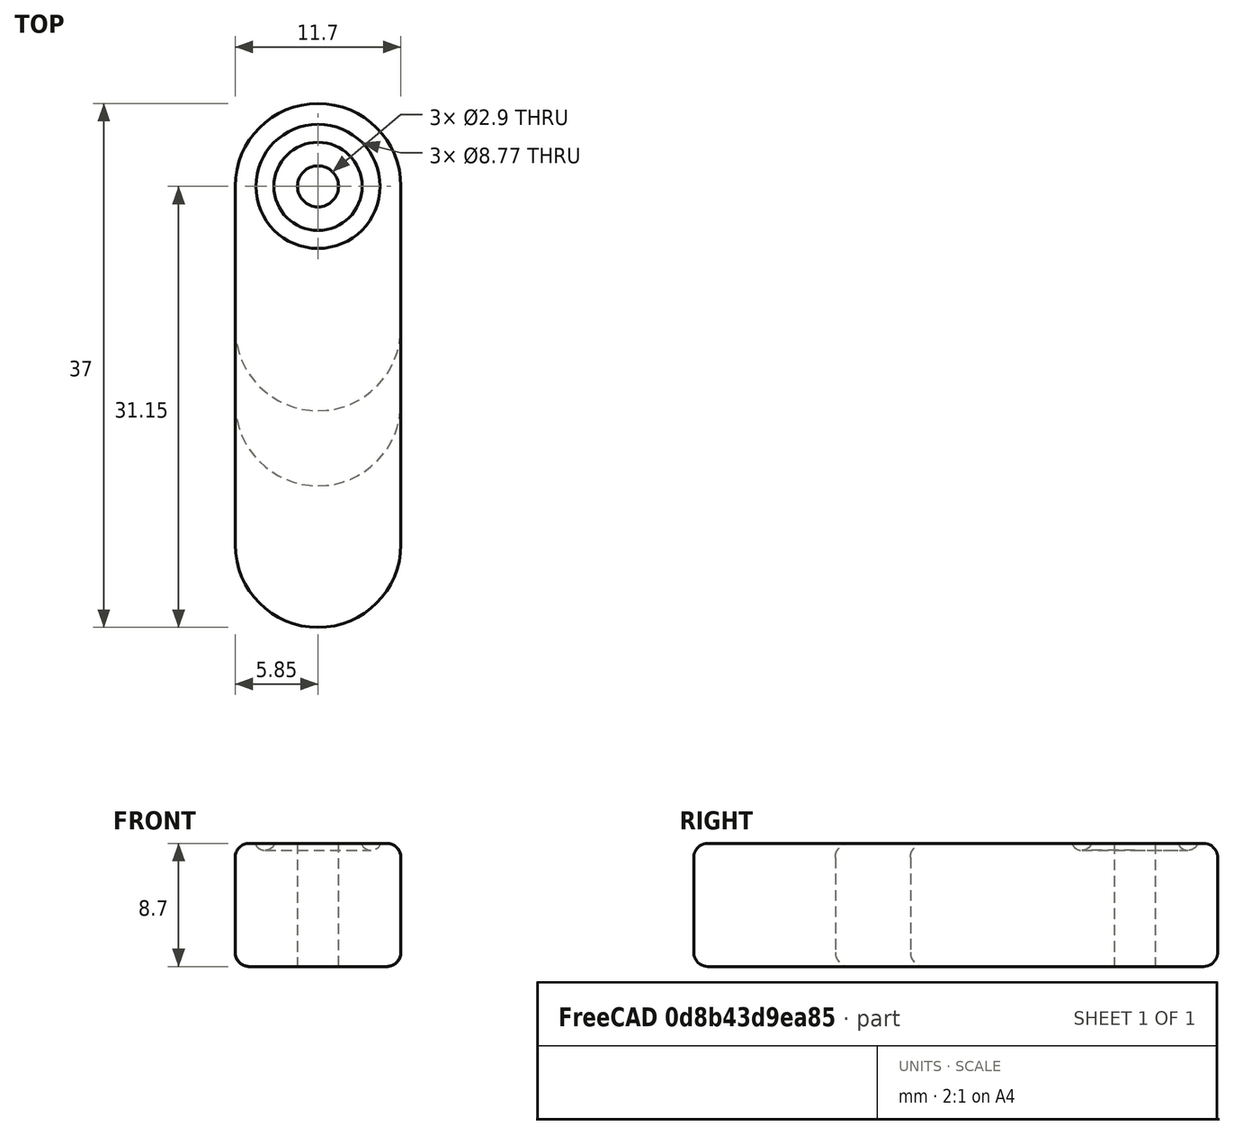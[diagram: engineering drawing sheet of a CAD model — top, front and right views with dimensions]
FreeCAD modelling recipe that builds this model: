
FCSTD DOCUMENT  (FreeCAD 1.0R39109 (Git))
Label: leg_very_small_six
License: All rights reserved
LicenseURL: http://en.wikipedia.org/wiki/All_rights_reserved
objects: Mesh::Feature×24, Sketcher::SketchObject×12, PartDesign::Groove×6, PartDesign::Fillet×6, PartDesign::Pad×3, PartDesign::Pocket×3, PartDesign::Body×3
note: 81 computed .brp shape members not serialized (recipe doc carries the construction recipe); baked Part::Feature solids carry a one-line shape summary decoded from their .brp

FEATURE [Sketcher::SketchObject] Sketch
  ArcFitTolerance = 0
  AttachmentSupport = -> [XY_Plane]
  FullyConstrained = true
  MakeInternals = false
  MapMode = 5
  sketch-geometry (4):
    g0: ArcOfCircle CenterX=0 CenterY=0 CenterZ=0 NormalX=0 NormalY=0 NormalZ=1 AngleXU=0 Radius=5.85 StartAngle=0 EndAngle=3.14159
    g1: LineSegment StartX=-5.85 StartY=7e-16 StartZ=0 EndX=-5.85 EndY=-10 EndZ=0
    g2: LineSegment StartX=5.85 StartY=0 StartZ=0 EndX=5.85 EndY=-10 EndZ=0
    g3: ArcOfCircle CenterX=3e-16 CenterY=-10 CenterZ=0 NormalX=0 NormalY=0 NormalZ=1 AngleXU=0 Radius=5.85 StartAngle=3.14159 EndAngle=6.28319
  constraints (12):
    c: Coincident(g0,g-1)
    c: PointOnObject(g0,g-1)
    c: PointOnObject(g0,g-1)
    c: Diameter(g0) = 11.7
    c: Coincident(g1,g0)
    c: Vertical(g1)
    c: Coincident(g2,g0)
    c: Vertical(g2)
    c: Equal(g2,g1)
    c: DistanceY(g1,g0) = 10
    c: Tangent(g1,g3) = -1.5708
    c: Coincident(g3,g2)
FEATURE [PartDesign::Pad] Pad
  Direction = (0,0,1)
  Length = 8.7
  Length2 = 10
  Profile = -> Sketch
  ReferenceAxis = -> Sketch [N_Axis]
  Suppressed = false
  Type = 0
FEATURE [Sketcher::SketchObject] Sketch001
  ArcFitTolerance = 0
  AttachmentSupport = -> [XY_Plane]
  FullyConstrained = true
  MakeInternals = false
  MapMode = 5
  sketch-geometry (1):
    g0: Circle CenterX=0 CenterY=0 CenterZ=0 NormalX=0 NormalY=0 NormalZ=1 AngleXU=0 Radius=1.45
  constraints (2):
    c: Coincident(g0,g-1)
    c: Diameter(g0) = 2.9
FEATURE [PartDesign::Pocket] Pocket
  BaseFeature = -> Pad
  Direction = (0,0,1)
  Length = 5
  Length2 = 5
  Profile = -> Sketch001
  ReferenceAxis = -> Sketch001 [N_Axis]
  Suppressed = false
  Type = 1
  UseCustomVector = true
FEATURE [Sketcher::SketchObject] Sketch002  label="elipse"
  ArcFitTolerance = 0
  AttachmentSupport = -> [XZ_Plane]
  FullyConstrained = true
  MakeInternals = false
  MapMode = 5
  Placement = pos=(0,0,0) rot=(1,0,0;1.5708rad)
  expr: Constraints[29] = 7.5 / 2
  sketch-geometry (13):
    g0: Circle [constr] CenterX=3.75 CenterY=8.7 CenterZ=0 NormalX=0 NormalY=0 NormalZ=1 AngleXU=0 Radius=0.5
    g1: LineSegment [constr] StartX=2.06 StartY=8.7 StartZ=0 EndX=5.44 EndY=8.7 EndZ=0
    g2: LineSegment [constr] StartX=3.75 StartY=6.89867 StartZ=0 EndX=3.75 EndY=10.0128 EndZ=0
    g3-g6: Circle [constr] x4 (B-spline internal-alignment scaffolding for g7; pole/knot coordinates omitted)
    g7: BSplineCurve PolesCount=4 KnotsCount=5 Degree=3 IsPeriodic=1
    g8-g12: GeomPoint [constr] x5 (B-spline internal-alignment scaffolding for g7; pole/knot coordinates omitted)
  constraints (23):
    c: Diameter(g0) = 1
    c: Horizontal(g1)
    c: PointOnObject(g0,g1)
    c: PointOnObject(g0,g2)
    c: Weight(g3) = 1
    c: PointOnObject(g3,g2)
    c: Equal(g3,g4)
    c: PointOnObject(g4,g1)
    c: Equal(g3,g5)
    c: PointOnObject(g5,g2)
    c: Equal(g3,g6)
    c: InternalAlignment(g3-g6 -> g7) x4
    c: InternalAlignment(g8-g12 -> g7) x5
    c: Symmetric(g1,g1,g2)
    c: Symmetric(g4,g6,g2)
    c: PointOnObject(g9,g0)
    c: Distance(g6,g3) = 1
    c: Distance(g11,g0) = 0.2
    c: Distance(g1,g2) = 2.47
    c: Distance(g2,g1) = 2.14
    c: Distance(g1,g0) = 1.69
    c: DistanceY(g-1,g0) = 8.7
    c: DistanceX(g-1,g0) = 3.75
FEATURE [PartDesign::Groove] Groove
  Angle = 360
  Angle2 = 60
  Axis = (0,2e-16,1)
  Base = (0,0,0)
  BaseFeature = -> Pocket
  Profile = -> Sketch002
  ReferenceAxis = -> Sketch002 [V_Axis]
  Suppressed = false
  Type = 0
FEATURE [Sketcher::SketchObject] Sketch003  label="rectangle"
  ArcFitTolerance = 0
  AttachmentSupport = -> [XZ_Plane]
  ExternalGeometry = -> [Sketch002]
  FullyConstrained = true
  MakeInternals = false
  MapMode = 5
  Placement = pos=(0,0,0) rot=(1,0,0;1.5708rad)
  sketch-geometry (4):
    g0: LineSegment StartX=3.11404 StartY=9.125 StartZ=0 EndX=4.38596 EndY=9.125 EndZ=0
    g1: LineSegment StartX=4.38596 StartY=9.125 StartZ=0 EndX=4.38596 EndY=8.625 EndZ=0
    g2: LineSegment StartX=4.38596 StartY=8.625 StartZ=0 EndX=3.11404 EndY=8.625 EndZ=0
    g3: LineSegment StartX=3.11404 StartY=8.625 StartZ=0 EndX=3.11404 EndY=9.125 EndZ=0
  constraints (11):
    c: Coincident(g0,g1)
    c: Coincident(g1,g2)
    c: Coincident(g2,g3)
    c: Coincident(g3,g0)
    c: Horizontal(g0)
    c: Horizontal(g2)
    c: Vertical(g1)
    c: Vertical(g3)
    c: Distance(g3) = 0.5
    c: Coincident(g2,g-3)
    c: PointOnObject(g1,g-3)
FEATURE [PartDesign::Groove] Groove001
  Angle = 360
  Angle2 = 60
  Axis = (0,2e-16,1)
  Base = (0,0,0)
  BaseFeature = -> Groove
  Profile = -> Sketch003
  ReferenceAxis = -> Sketch003 [V_Axis]
  Suppressed = false
  Type = 0
FEATURE [PartDesign::Fillet] Fillet
  Base = -> Groove001 [Edge10]
  BaseFeature = -> Groove001
  Radius = 1
  SupportTransform = false
  Suppressed = false
  UseAllEdges = false
FEATURE [PartDesign::Fillet] Fillet001
  Base = -> Fillet [Edge12]
  BaseFeature = -> Fillet
  Radius = 1
  SupportTransform = false
  Suppressed = false
  UseAllEdges = false
FEATURE [PartDesign::Body] Body  label="leg_22mm"
  AllowCompound = false
  Group = -> [Sketch,Pad,Sketch001,Pocket,Sketch002,Groove,Sketch003,Groove001,Fillet,Fillet001]
  Origin = -> Origin
  Tip = -> Fillet001
FEATURE [Mesh::Feature] Mesh  label="leg_22 001"
FEATURE [Mesh::Feature] Mesh001  label="leg_22 002"
  Placement = pos=(15,0,0) rot=(0,0,1;0rad)
FEATURE [Mesh::Feature] Mesh002  label="leg_22 003"
  Placement = pos=(30,0,0) rot=(0,0,1;0rad)
FEATURE [Mesh::Feature] Mesh003  label="leg_22 004"
  Placement = pos=(0,24,0) rot=(0,0,1;0rad)
FEATURE [Mesh::Feature] Mesh004  label="leg_22 005"
  Placement = pos=(15,24,0) rot=(0,0,1;0rad)
FEATURE [Mesh::Feature] Mesh005  label="leg_22 006"
  Placement = pos=(30,24,0) rot=(0,0,1;0rad)
FEATURE [Sketcher::SketchObject] Sketch004
  ArcFitTolerance = 0
  AttachmentSupport = -> [XY_Plane001]
  FullyConstrained = true
  MakeInternals = false
  MapMode = 5
  sketch-geometry (4):
    g0: ArcOfCircle CenterX=0 CenterY=0 CenterZ=0 NormalX=0 NormalY=0 NormalZ=1 AngleXU=0 Radius=5.85 StartAngle=0 EndAngle=3.14159
    g1: LineSegment StartX=-5.85 StartY=7e-16 StartZ=0 EndX=-5.85 EndY=-15.3 EndZ=0
    g2: LineSegment StartX=5.85 StartY=0 StartZ=0 EndX=5.85 EndY=-15.3 EndZ=0
    g3: ArcOfCircle CenterX=1.355e-13 CenterY=-15.3 CenterZ=0 NormalX=0 NormalY=0 NormalZ=1 AngleXU=0 Radius=5.85 StartAngle=3.14159 EndAngle=6.28319
  constraints (12):
    c: Coincident(g0,g-1)
    c: PointOnObject(g0,g-1)
    c: PointOnObject(g0,g-1)
    c: Diameter(g0) = 11.7
    c: Coincident(g1,g0)
    c: Vertical(g1)
    c: Coincident(g2,g0)
    c: Vertical(g2)
    c: Equal(g2,g1)
    c: DistanceY(g1,g0) = 15.3
    c: Tangent(g1,g3) = -1.5708
    c: Coincident(g3,g2)
FEATURE [PartDesign::Pad] Pad001
  Direction = (0,0,1)
  Length = 8.7
  Length2 = 10
  Profile = -> Sketch004
  ReferenceAxis = -> Sketch004 [N_Axis]
  Suppressed = false
  Type = 0
FEATURE [Sketcher::SketchObject] Sketch005
  ArcFitTolerance = 0
  AttachmentSupport = -> [XY_Plane001]
  FullyConstrained = true
  MakeInternals = false
  MapMode = 5
  sketch-geometry (1):
    g0: Circle CenterX=0 CenterY=0 CenterZ=0 NormalX=0 NormalY=0 NormalZ=1 AngleXU=0 Radius=1.45
  constraints (2):
    c: Coincident(g0,g-1)
    c: Diameter(g0) = 2.9
FEATURE [PartDesign::Pocket] Pocket001
  BaseFeature = -> Pad001
  Direction = (0,0,1)
  Length = 5
  Length2 = 5
  Profile = -> Sketch005
  ReferenceAxis = -> Sketch005 [N_Axis]
  Suppressed = false
  Type = 1
  UseCustomVector = true
FEATURE [Sketcher::SketchObject] Sketch006  label="elipse001"
  ArcFitTolerance = 0
  AttachmentSupport = -> [XZ_Plane001]
  FullyConstrained = true
  MakeInternals = false
  MapMode = 5
  Placement = pos=(0,0,0) rot=(1,0,0;1.5708rad)
  expr: Constraints[29] = 7.5 / 2
  sketch-geometry (13):
    g0: Circle [constr] CenterX=3.75 CenterY=8.7 CenterZ=0 NormalX=0 NormalY=0 NormalZ=1 AngleXU=0 Radius=0.5
    g1: LineSegment [constr] StartX=2.06 StartY=8.7 StartZ=0 EndX=5.44 EndY=8.7 EndZ=0
    g2: LineSegment [constr] StartX=3.75 StartY=6.89867 StartZ=0 EndX=3.75 EndY=10.0128 EndZ=0
    g3-g6: Circle [constr] x4 (B-spline internal-alignment scaffolding for g7; pole/knot coordinates omitted)
    g7: BSplineCurve PolesCount=4 KnotsCount=5 Degree=3 IsPeriodic=1
    g8-g12: GeomPoint [constr] x5 (B-spline internal-alignment scaffolding for g7; pole/knot coordinates omitted)
  constraints (23):
    c: Diameter(g0) = 1
    c: Horizontal(g1)
    c: PointOnObject(g0,g1)
    c: PointOnObject(g0,g2)
    c: Weight(g3) = 1
    c: PointOnObject(g3,g2)
    c: Equal(g3,g4)
    c: PointOnObject(g4,g1)
    c: Equal(g3,g5)
    c: PointOnObject(g5,g2)
    c: Equal(g3,g6)
    c: InternalAlignment(g3-g6 -> g7) x4
    c: InternalAlignment(g8-g12 -> g7) x5
    c: Symmetric(g1,g1,g2)
    c: Symmetric(g4,g6,g2)
    c: PointOnObject(g9,g0)
    c: Distance(g6,g3) = 1
    c: Distance(g11,g0) = 0.2
    c: Distance(g1,g2) = 2.47
    c: Distance(g2,g1) = 2.14
    c: Distance(g1,g0) = 1.69
    c: DistanceY(g-1,g0) = 8.7
    c: DistanceX(g-1,g0) = 3.75
FEATURE [PartDesign::Groove] Groove002
  Angle = 360
  Angle2 = 60
  Axis = (0,2e-16,1)
  Base = (0,0,0)
  BaseFeature = -> Pocket001
  Profile = -> Sketch006
  ReferenceAxis = -> Sketch006 [V_Axis]
  Suppressed = false
  Type = 0
FEATURE [Sketcher::SketchObject] Sketch007  label="rectangle001"
  ArcFitTolerance = 0
  AttachmentSupport = -> [XZ_Plane001]
  ExternalGeometry = -> [Sketch006]
  FullyConstrained = true
  MakeInternals = false
  MapMode = 5
  Placement = pos=(0,0,0) rot=(1,0,0;1.5708rad)
  sketch-geometry (4):
    g0: LineSegment StartX=3.11404 StartY=9.125 StartZ=0 EndX=4.38596 EndY=9.125 EndZ=0
    g1: LineSegment StartX=4.38596 StartY=9.125 StartZ=0 EndX=4.38596 EndY=8.625 EndZ=0
    g2: LineSegment StartX=4.38596 StartY=8.625 StartZ=0 EndX=3.11404 EndY=8.625 EndZ=0
    g3: LineSegment StartX=3.11404 StartY=8.625 StartZ=0 EndX=3.11404 EndY=9.125 EndZ=0
  constraints (11):
    c: Coincident(g0,g1)
    c: Coincident(g1,g2)
    c: Coincident(g2,g3)
    c: Coincident(g3,g0)
    c: Horizontal(g0)
    c: Horizontal(g2)
    c: Vertical(g1)
    c: Vertical(g3)
    c: Distance(g3) = 0.5
    c: Coincident(g2,g-3)
    c: PointOnObject(g1,g-3)
FEATURE [PartDesign::Groove] Groove003
  Angle = 360
  Angle2 = 60
  Axis = (0,2e-16,1)
  Base = (0,0,0)
  BaseFeature = -> Groove002
  Profile = -> Sketch007
  ReferenceAxis = -> Sketch007 [V_Axis]
  Suppressed = false
  Type = 0
FEATURE [PartDesign::Fillet] Fillet002
  Base = -> Groove003 [Edge10]
  BaseFeature = -> Groove003
  Radius = 1
  SupportTransform = false
  Suppressed = false
  UseAllEdges = false
FEATURE [PartDesign::Fillet] Fillet003
  Base = -> Fillet002 [Edge12]
  BaseFeature = -> Fillet002
  Radius = 1
  SupportTransform = false
  Suppressed = false
  UseAllEdges = false
FEATURE [PartDesign::Body] Body001  label="leg_27mm"
  AllowCompound = false
  Group = -> [Sketch004,Pad001,Sketch005,Pocket001,Sketch006,Groove002,Sketch007,Groove003,Fillet002,Fillet003]
  Origin = -> Origin001
  Tip = -> Fillet003
FEATURE [Sketcher::SketchObject] Sketch008
  ArcFitTolerance = 0
  AttachmentSupport = -> [XY_Plane002]
  FullyConstrained = true
  MakeInternals = false
  MapMode = 5
  sketch-geometry (4):
    g0: ArcOfCircle CenterX=0 CenterY=0 CenterZ=0 NormalX=0 NormalY=0 NormalZ=1 AngleXU=0 Radius=5.85 StartAngle=0 EndAngle=3.14159
    g1: LineSegment StartX=-5.85 StartY=7e-16 StartZ=0 EndX=-5.85 EndY=-25.3 EndZ=0
    g2: LineSegment StartX=5.85 StartY=0 StartZ=0 EndX=5.85 EndY=-25.3 EndZ=0
    g3: ArcOfCircle CenterX=1.0394e-12 CenterY=-25.3 CenterZ=0 NormalX=0 NormalY=0 NormalZ=1 AngleXU=0 Radius=5.85 StartAngle=3.14159 EndAngle=6.28319
  constraints (12):
    c: Coincident(g0,g-1)
    c: PointOnObject(g0,g-1)
    c: PointOnObject(g0,g-1)
    c: Diameter(g0) = 11.7
    c: Coincident(g1,g0)
    c: Vertical(g1)
    c: Coincident(g2,g0)
    c: Vertical(g2)
    c: Equal(g2,g1)
    c: DistanceY(g1,g0) = 25.3
    c: Tangent(g1,g3) = -1.5708
    c: Coincident(g3,g2)
FEATURE [PartDesign::Pad] Pad002
  Direction = (0,0,1)
  Length = 8.7
  Length2 = 10
  Profile = -> Sketch008
  ReferenceAxis = -> Sketch008 [N_Axis]
  Suppressed = false
  Type = 0
FEATURE [Sketcher::SketchObject] Sketch009
  ArcFitTolerance = 0
  AttachmentSupport = -> [XY_Plane002]
  FullyConstrained = true
  MakeInternals = false
  MapMode = 5
  sketch-geometry (1):
    g0: Circle CenterX=0 CenterY=0 CenterZ=0 NormalX=0 NormalY=0 NormalZ=1 AngleXU=0 Radius=1.45
  constraints (2):
    c: Coincident(g0,g-1)
    c: Diameter(g0) = 2.9
FEATURE [PartDesign::Pocket] Pocket002
  BaseFeature = -> Pad002
  Direction = (0,0,1)
  Length = 5
  Length2 = 5
  Profile = -> Sketch009
  ReferenceAxis = -> Sketch009 [N_Axis]
  Suppressed = false
  Type = 1
  UseCustomVector = true
FEATURE [Sketcher::SketchObject] Sketch010  label="elipse002"
  ArcFitTolerance = 0
  AttachmentSupport = -> [XZ_Plane002]
  FullyConstrained = true
  MakeInternals = false
  MapMode = 5
  Placement = pos=(0,0,0) rot=(1,0,0;1.5708rad)
  expr: Constraints[29] = 7.5 / 2
  sketch-geometry (13):
    g0: Circle [constr] CenterX=3.75 CenterY=8.7 CenterZ=0 NormalX=0 NormalY=0 NormalZ=1 AngleXU=0 Radius=0.5
    g1: LineSegment [constr] StartX=2.06 StartY=8.7 StartZ=0 EndX=5.44 EndY=8.7 EndZ=0
    g2: LineSegment [constr] StartX=3.75 StartY=6.89867 StartZ=0 EndX=3.75 EndY=10.0128 EndZ=0
    g3-g6: Circle [constr] x4 (B-spline internal-alignment scaffolding for g7; pole/knot coordinates omitted)
    g7: BSplineCurve PolesCount=4 KnotsCount=5 Degree=3 IsPeriodic=1
    g8-g12: GeomPoint [constr] x5 (B-spline internal-alignment scaffolding for g7; pole/knot coordinates omitted)
  constraints (23):
    c: Diameter(g0) = 1
    c: Horizontal(g1)
    c: PointOnObject(g0,g1)
    c: PointOnObject(g0,g2)
    c: Weight(g3) = 1
    c: PointOnObject(g3,g2)
    c: Equal(g3,g4)
    c: PointOnObject(g4,g1)
    c: Equal(g3,g5)
    c: PointOnObject(g5,g2)
    c: Equal(g3,g6)
    c: InternalAlignment(g3-g6 -> g7) x4
    c: InternalAlignment(g8-g12 -> g7) x5
    c: Symmetric(g1,g1,g2)
    c: Symmetric(g4,g6,g2)
    c: PointOnObject(g9,g0)
    c: Distance(g6,g3) = 1
    c: Distance(g11,g0) = 0.2
    c: Distance(g1,g2) = 2.47
    c: Distance(g2,g1) = 2.14
    c: Distance(g1,g0) = 1.69
    c: DistanceY(g-1,g0) = 8.7
    c: DistanceX(g-1,g0) = 3.75
FEATURE [PartDesign::Groove] Groove004
  Angle = 360
  Angle2 = 60
  Axis = (0,2e-16,1)
  Base = (0,0,0)
  BaseFeature = -> Pocket002
  Profile = -> Sketch010
  ReferenceAxis = -> Sketch010 [V_Axis]
  Suppressed = false
  Type = 0
FEATURE [Sketcher::SketchObject] Sketch011  label="rectangle002"
  ArcFitTolerance = 0
  AttachmentSupport = -> [XZ_Plane002]
  ExternalGeometry = -> [Sketch010]
  FullyConstrained = true
  MakeInternals = false
  MapMode = 5
  Placement = pos=(0,0,0) rot=(1,0,0;1.5708rad)
  sketch-geometry (4):
    g0: LineSegment StartX=3.11404 StartY=9.125 StartZ=0 EndX=4.38596 EndY=9.125 EndZ=0
    g1: LineSegment StartX=4.38596 StartY=9.125 StartZ=0 EndX=4.38596 EndY=8.625 EndZ=0
    g2: LineSegment StartX=4.38596 StartY=8.625 StartZ=0 EndX=3.11404 EndY=8.625 EndZ=0
    g3: LineSegment StartX=3.11404 StartY=8.625 StartZ=0 EndX=3.11404 EndY=9.125 EndZ=0
  constraints (11):
    c: Coincident(g0,g1)
    c: Coincident(g1,g2)
    c: Coincident(g2,g3)
    c: Coincident(g3,g0)
    c: Horizontal(g0)
    c: Horizontal(g2)
    c: Vertical(g1)
    c: Vertical(g3)
    c: Distance(g3) = 0.5
    c: Coincident(g2,g-3)
    c: PointOnObject(g1,g-3)
FEATURE [PartDesign::Groove] Groove005
  Angle = 360
  Angle2 = 60
  Axis = (0,2e-16,1)
  Base = (0,0,0)
  BaseFeature = -> Groove004
  Profile = -> Sketch011
  ReferenceAxis = -> Sketch011 [V_Axis]
  Suppressed = false
  Type = 0
FEATURE [PartDesign::Fillet] Fillet004
  Base = -> Groove005 [Edge10]
  BaseFeature = -> Groove005
  Radius = 1
  SupportTransform = false
  Suppressed = false
  UseAllEdges = false
FEATURE [PartDesign::Fillet] Fillet005
  Base = -> Fillet004 [Edge12]
  BaseFeature = -> Fillet004
  Radius = 1
  SupportTransform = false
  Suppressed = false
  UseAllEdges = false
FEATURE [PartDesign::Body] Body002  label="leg_36mm"
  AllowCompound = false
  Group = -> [Sketch008,Pad002,Sketch009,Pocket002,Sketch010,Groove004,Sketch011,Groove005,Fillet004,Fillet005]
  Origin = -> Origin002
  Tip = -> Fillet005
FEATURE [Mesh::Feature] Mesh006  label="leg_27mm 001"
  Placement = pos=(0,-30,0) rot=(0,0,1;0rad)
FEATURE [Mesh::Feature] Mesh012  label="leg_36mm 001"
  Placement = pos=(0,-90,0) rot=(0,0,1;0rad)
FEATURE [Mesh::Feature] Mesh018  label="leg_22 007"
  Placement = pos=(45,24,0) rot=(0,0,1;0rad)
FEATURE [Mesh::Feature] Mesh020  label="leg_27mm 002"
  Placement = pos=(15,-30,0) rot=(0,0,1;0rad)
FEATURE [Mesh::Feature] Mesh021  label="leg_27mm 003"
  Placement = pos=(30,-30,0) rot=(0,0,1;0rad)
FEATURE [Mesh::Feature] Mesh022  label="leg_27mm 004"
  Placement = pos=(45,-30,0) rot=(0,0,1;0rad)
FEATURE [Mesh::Feature] Mesh023  label="leg_27mm 005"
  Placement = pos=(0,-60,0) rot=(0,0,1;0rad)
FEATURE [Mesh::Feature] Mesh034  label="leg_22 008"
  Placement = pos=(45,0,0) rot=(0,0,1;0rad)
FEATURE [Mesh::Feature] Mesh035  label="leg_27mm 006"
  Placement = pos=(15,-60,0) rot=(0,0,1;0rad)
FEATURE [Mesh::Feature] Mesh036  label="leg_27mm 007"
  Placement = pos=(30,-60,0) rot=(0,0,1;0rad)
FEATURE [Mesh::Feature] Mesh037  label="leg_27mm 008"
  Placement = pos=(45,-60,0) rot=(0,0,1;0rad)
FEATURE [Mesh::Feature] Mesh038  label="leg_36mm 002"
  Placement = pos=(15,-90,0) rot=(0,0,1;0rad)
FEATURE [Mesh::Feature] Mesh039  label="leg_36mm 003"
  Placement = pos=(30,-90,0) rot=(0,0,1;0rad)
FEATURE [Mesh::Feature] Mesh040  label="leg_36mm 004"
  Placement = pos=(45,-90,0) rot=(0,0,1;0rad)
FEATURE [Mesh::Feature] Mesh041  label="leg_36mm 005"
  Placement = pos=(0,-130,0) rot=(0,0,1;0rad)
FEATURE [Mesh::Feature] Mesh042  label="leg_36mm 006"
  Placement = pos=(15,-130,0) rot=(0,0,1;0rad)
FEATURE [Mesh::Feature] Mesh043  label="leg_36mm 007"
  Placement = pos=(30,-130,0) rot=(0,0,1;0rad)
FEATURE [Mesh::Feature] Mesh044  label="leg_36mm 008"
  Placement = pos=(45,-130,0) rot=(0,0,1;0rad)
